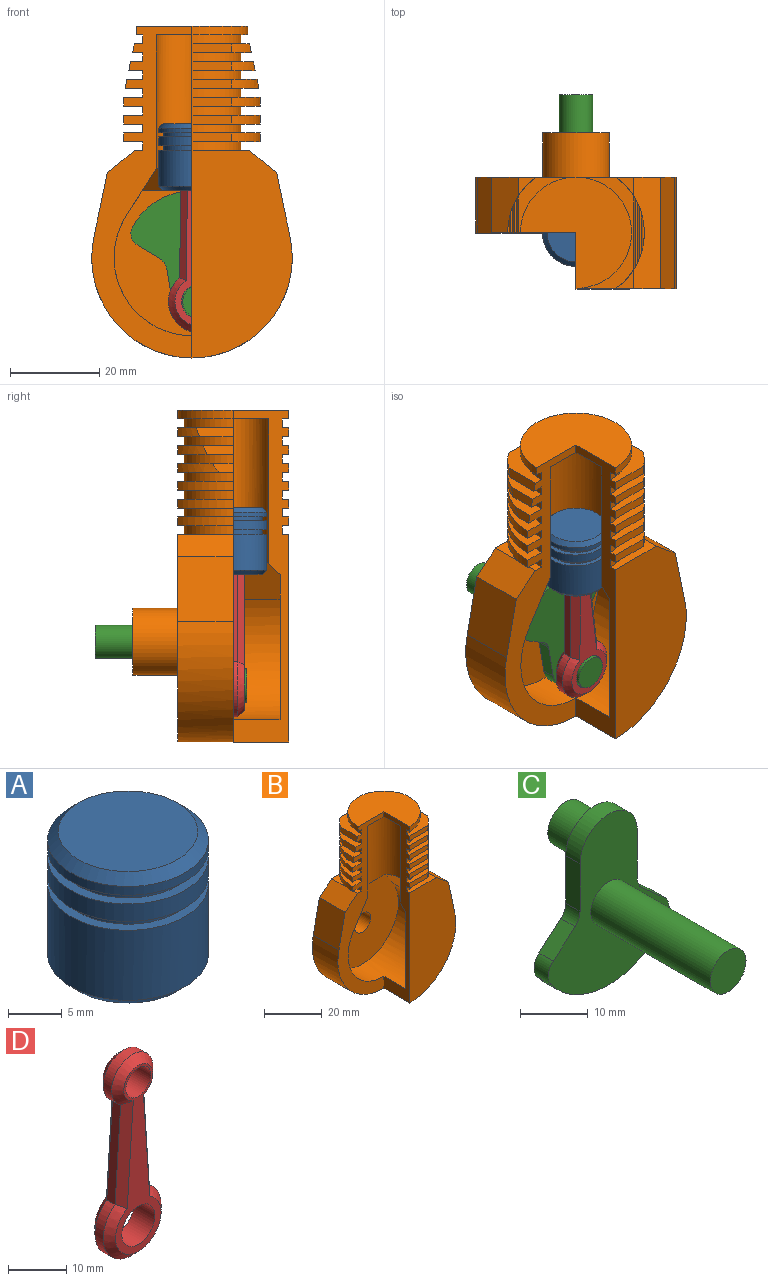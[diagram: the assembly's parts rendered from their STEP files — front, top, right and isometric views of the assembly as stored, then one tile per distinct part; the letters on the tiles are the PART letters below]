
ASSEMBLY  parts=4 mates=6
PART A: 23 faces, bbox 15x15x15 mm
  f0: plane 13x13mm, normal (0,0,-1), area 68.7mm2, adj f11,f12,f13,f14,f17,f19,f20,f21
  f1: cylinder r=7.5mm len=15mm, axis (0,0,-1), area 377mm2, adj f2,f17
  f2: plane 15x15mm, normal (0,0,1), area 44mm2, adj f1,f3
  f3: cylinder r=6.5mm len=13mm, axis (0,0,-1), area 40.8mm2, adj f2,f4
  f4: plane 15x15mm, normal (0,0,-1), area 44mm2, adj f3,f5
  f5: cylinder r=7.5mm len=15mm, axis (0,0,-1), area 94.2mm2, adj f4,f6
  f6: plane 15x15mm, normal (0,0,1), area 44mm2, adj f5,f7
  f7: cylinder r=6.5mm len=13mm, axis (0,0,-1), area 40.8mm2, adj f6,f8
  f8: plane 15x15mm, normal (0,0,-1), area 44mm2, adj f7,f9
  f9: cylinder r=7.5mm len=15mm, axis (0,0,-1), area 47.1mm2, adj f8,f18
  f10: plane 13x13mm, normal (0,0,1), area 132.7mm2, adj f18
  f11: plane 12x4mm, normal (0,1,0), area 48mm2, adj f0,f15,f21,f22
  f12: plane 12x9mm, normal (1,0,0), area 84.2mm2, adj f0,f15,f16,f20,f21
  f13: plane 12x4mm, normal (0,-1,0), area 48mm2, adj f0,f15,f19,f20
  f14: plane 12x9mm, normal (-1,0,0), area 84.2mm2, adj f0,f15,f16,f19,f22
  f15: plane 11x6mm, normal (0,0,-1), area 64mm2, adj f11,f12,f13,f14,f19,f20,f21,f22
  f16: cylinder r=2.75mm len=6mm, axis (-1,0,0), area 103.7mm2, adj f12,f14
  f17: cone r=6.5mm half-angle=45deg, axis (0,0,1), area 62.2mm2, adj f0,f1
  f18: cone r=7.5mm half-angle=45deg, axis (0,0,-1), area 62.2mm2, adj f9,f10
  f19: plane 12x1mm, normal (-0.71,-0.71,0), area 17mm2, adj f0,f13,f14,f15
  f20: plane 12x1mm, normal (0.71,-0.71,0), area 17mm2, adj f0,f12,f13,f15
  f21: plane 12x1mm, normal (0.71,0.71,0), area 17mm2, adj f0,f11,f12,f15
  f22: plane 12x1mm, normal (-0.71,0.71,0), area 17mm2, adj f0,f11,f14,f15
PART B: 80 faces, bbox 45x35x74.5 mm
  f0: plane 74.5x22.5mm, normal (0,-1,0), area 473.4mm2, adj f8,f12,f16,f19,f20,f21,f22,f23
  f1: plane 8.89x2mm, normal (0,-1,0), area 17.8mm2, adj f28,f30,f35,f59
  f2: plane 17.77x2mm, normal (0,1,0), area 35.5mm2, adj f28,f30,f59,f60
  f3: plane 8.89x2mm, normal (0,-1,0), area 17.8mm2, adj f26,f29,f35,f61
  f4: plane 17.77x2mm, normal (0,1,0), area 35.5mm2, adj f26,f29,f61,f62
  f5: plane 8.89x2mm, normal (0,-1,0), area 17.8mm2, adj f24,f27,f35,f63
  f6: plane 17.77x2mm, normal (0,1,0), area 35.5mm2, adj f24,f27,f63,f64
  f7: plane 8.89x2mm, normal (0,-1,0), area 17.8mm2, adj f22,f25,f35,f65
  f8: plane 4.7x2mm, normal (-0.98,0,0.21), area 8.1mm2, adj f0,f22,f25,f66
  f9: plane 9.4x2mm, normal (0.98,0,0.21), area 16.2mm2, adj f22,f25,f65,f67
  f10: plane 17.77x2mm, normal (0,1,0), area 35.5mm2, adj f22,f25,f66,f67
  f11: plane 8.89x2mm, normal (0,-1,0), area 17.8mm2, adj f20,f23,f35,f68
  f12: plane 6.77x2mm, normal (-0.98,0,0.21), area 12.9mm2, adj f0,f20,f23,f69
  f13: plane 13.55x2mm, normal (0.98,0,0.21), area 25.8mm2, adj f20,f23,f68,f70
  f14: plane 17.77x2mm, normal (0,1,0), area 35.5mm2, adj f20,f23,f69,f70
  f15: plane 8.89x2mm, normal (0,-1,0), area 17.8mm2, adj f19,f21,f35,f71
  f16: plane 8.26x2mm, normal (-0.98,0,0.21), area 16.2mm2, adj f0,f19,f21,f72
  f17: plane 16.53x2mm, normal (0.98,0,0.21), area 32.4mm2, adj f19,f21,f71,f73
  f18: plane 17.77x2mm, normal (0,1,0), area 35.5mm2, adj f19,f21,f72,f73
  f19: plane 25.84x25mm, normal (0,0,1), area 177mm2, adj f0,f15,f16,f17,f18,f35,f51,f71
  f20: plane 27.52x25mm, normal (0,0,1), area 196.1mm2, adj f0,f11,f12,f13,f14,f35,f52,f68
  f21: plane 26.68x25mm, normal (0,0,-1), area 187mm2, adj f0,f15,f16,f17,f18,f35,f52,f71
  f22: plane 29.2x25mm, normal (0,0,1), area 210.7mm2, adj f0,f7,f8,f9,f10,f35,f53,f65
  f23: plane 28.36x25mm, normal (0,0,-1), area 204mm2, adj f0,f11,f12,f13,f14,f35,f53,f68
  f24: plane 30.67x25mm, normal (0,0,1), area 217.7mm2, adj f0,f5,f6,f35,f54,f63,f64
  f25: plane 30.04x25mm, normal (0,0,-1), area 215.7mm2, adj f0,f7,f8,f9,f10,f35,f54,f65
  f26: plane 30.67x25mm, normal (0,0,1), area 217.7mm2, adj f0,f3,f4,f35,f55,f61,f62
  f27: plane 30.67x25mm, normal (0,0,-1), area 217.7mm2, adj f0,f5,f6,f35,f55,f63,f64
  f28: plane 30.67x25mm, normal (0,0,1), area 217.7mm2, adj f0,f1,f2,f35,f56,f59,f60
  f29: plane 30.67x25mm, normal (0,0,-1), area 217.7mm2, adj f0,f3,f4,f35,f56,f61,f62
  f30: plane 30.67x25mm, normal (0,0,-1), area 217.7mm2, adj f0,f1,f2,f35,f57,f59,f60
  f31: plane 46.5x22.5mm, normal (0,-1,0), area 875.9mm2, adj f33,f35,f45,f58,f75
  f32: plane 14.49x12.5mm, normal (-0.98,0,0.21), area 185mm2, adj f0,f34,f45,f74
  f33: plane 25x14.49mm, normal (0.98,0,0.21), area 370.1mm2, adj f31,f34,f45,f75
  f34: plane 46.5x45mm, normal (0,1,0), area 1575.2mm2, adj f32,f33,f43,f45,f58,f74,f75
  f35: plane 74.5x12.5mm, normal (-1,0,0), area 285.8mm2, adj f0,f1,f3,f5,f7,f11,f15,f19
  f36: plane 5.5x2.19mm, normal (0,0,-1), area 3.8mm2, adj f39,f42,f50
  f37: plane 5.5x2.19mm, normal (0,0,-1), area 3.8mm2, adj f38,f42,f49
  f38: plane 21x10.59mm, normal (-0.84,0,-0.54), area 234.1mm2, adj f37,f40,f46,f47,f48,f49,f50
  f39: plane 10.59x10.5mm, normal (0.84,0,-0.54), area 117.1mm2, adj f0,f36,f40,f47,f50
  f40: cylinder r=17.5mm len=35mm, axis (0,-1,0), area 1178.9mm2, adj f0,f35,f38,f39,f47,f48
  f41: cylinder r=4mm len=12mm, axis (0,1,0), area 301.6mm2, adj f44,f47
  f42: cylinder r=8mm len=32.51mm, axis (0,0,1), area 1163.1mm2, adj f0,f35,f36,f37,f46,f49,f50,f76
  f43: cylinder r=7.5mm len=15mm, axis (0,1,0), area 471.2mm2, adj f34,f44
  f44: plane 15x15mm, normal (0,1,0), area 126.4mm2, adj f41,f43
  f45: cylinder r=22.5mm len=45mm, axis (0,1,0), area 1499.8mm2, adj f0,f31,f32,f33,f34,f35
  f46: plane 5.5x2.19mm, normal (0,0,-1), area 3.8mm2, adj f38,f42,f50
  f47: plane 35x32.5mm, normal (0,-1,0), area 888.5mm2, adj f38,f39,f40,f41,f50
  f48: plane 32.5x17.5mm, normal (0,1,0), area 469.4mm2, adj f35,f38,f40,f49
  f49: plane 11.19x5mm, normal (0,0.71,-0.71), area 53.7mm2, adj f35,f37,f38,f42,f48
  f50: plane 22.38x5mm, normal (0,-0.71,-0.71), area 107.3mm2, adj f36,f38,f39,f42,f46,f47
  f51: cylinder r=11mm len=22mm, axis (0,0,1), area 103.7mm2, adj f0,f19,f35,f79
  f52: cylinder r=11mm len=22mm, axis (0,0,1), area 103.7mm2, adj f0,f20,f21,f35
  f53: cylinder r=11mm len=22mm, axis (0,0,1), area 103.7mm2, adj f0,f22,f23,f35
  f54: cylinder r=11mm len=22mm, axis (0,0,1), area 103.7mm2, adj f0,f24,f25,f35
  f55: cylinder r=11mm len=22mm, axis (0,0,1), area 103.7mm2, adj f0,f26,f27,f35
  f56: cylinder r=11mm len=22mm, axis (0,0,1), area 103.7mm2, adj f0,f28,f29,f35
  f57: cylinder r=11mm len=22mm, axis (0,0,1), area 103.7mm2, adj f0,f30,f35,f58
  f58: plane 25.91x25mm, normal (0,0,1), area 200.7mm2, adj f0,f31,f34,f35,f57,f74,f75
  f59: cylinder r=15.34mm len=25mm, axis (0,0,1), area 58.5mm2, adj f1,f2,f28,f30
  f60: cylinder r=15.34mm len=12.5mm, axis (0,0,1), area 29.2mm2, adj f0,f2,f28,f30
  f61: cylinder r=15.34mm len=25mm, axis (0,0,1), area 58.5mm2, adj f3,f4,f26,f29
  f62: cylinder r=15.34mm len=12.5mm, axis (0,0,1), area 29.2mm2, adj f0,f4,f26,f29
  f63: cylinder r=15.34mm len=25mm, axis (0,0,1), area 58.5mm2, adj f5,f6,f24,f27
  f64: cylinder r=15.34mm len=12.5mm, axis (0,0,1), area 29.2mm2, adj f0,f6,f24,f27
  f65: cylinder r=15.34mm len=9.39mm, axis (0,0,1), area 21.2mm2, adj f7,f9,f22,f25
  f66: cylinder r=15.34mm len=9.39mm, axis (0,0,1), area 21.2mm2, adj f8,f10,f22,f25
  f67: cylinder r=15.34mm len=9.39mm, axis (0,0,1), area 21.2mm2, adj f9,f10,f22,f25
  f68: cylinder r=15.34mm len=6.65mm, axis (0,0,1), area 16.2mm2, adj f11,f13,f20,f23
  f69: cylinder r=15.34mm len=6.65mm, axis (0,0,1), area 16.2mm2, adj f12,f14,f20,f23
  f70: cylinder r=15.34mm len=6.65mm, axis (0,0,1), area 16.2mm2, adj f13,f14,f20,f23
  f71: cylinder r=15.34mm len=4.93mm, axis (0,0,1), area 12.6mm2, adj f15,f17,f19,f21
  f72: cylinder r=15.34mm len=4.93mm, axis (0,0,1), area 12.6mm2, adj f16,f18,f19,f21
  f73: cylinder r=15.34mm len=4.93mm, axis (0,0,1), area 12.6mm2, adj f17,f18,f19,f21
  f74: plane 12.5x6.03mm, normal (-0.63,0,0.78), area 97mm2, adj f0,f32,f34,f58
  f75: plane 25x6.03mm, normal (0.63,0,0.78), area 194.1mm2, adj f31,f33,f34,f58
  f76: plane 16x16mm, normal (0,0,-1), area 150.8mm2, adj f0,f35,f42
  f77: cylinder r=12.48mm len=24.97mm, axis (0,0,-1), area 117.7mm2, adj f0,f35,f78,f79
  f78: plane 24.97x24.97mm, normal (0,0,1), area 367.2mm2, adj f0,f35,f77
  f79: plane 24.97x24.97mm, normal (0,0,-1), area 82.1mm2, adj f0,f35,f51,f77
PART C: 16 faces, bbox 25.3x34x31 mm
  f0: cylinder r=3.75mm len=7.5mm, axis (0,1,0), area 141.4mm2, adj f1,f9
  f1: plane 7.5x7.5mm, normal (0,1,0), area 44.2mm2, adj f0
  f2: plane 8.63x3mm, normal (-1,0,0), area 25.9mm2, adj f7,f8,f9,f12
  f3: plane 4.58x3.99mm, normal (-0.66,0,0.75), area 18.2mm2, adj f8,f9,f12,f14
  f4: cylinder r=15mm len=24.1mm, axis (0,1,0), area 84mm2, adj f8,f9,f14,f15
  f5: plane 4.58x3.99mm, normal (0.66,0,0.75), area 18.2mm2, adj f8,f9,f13,f15
  f6: plane 8.63x3mm, normal (1,0,0), area 25.9mm2, adj f7,f8,f9,f13
  f7: cylinder r=6mm len=12mm, axis (0,1,0), area 56.5mm2, adj f2,f6,f8,f9
  f8: plane 31x25.28mm, normal (0,-1,0), area 421.4mm2, adj f2,f3,f4,f5,f6,f7,f10,f12
  f9: plane 31x25.28mm, normal (0,1,0), area 421.4mm2, adj f0,f2,f3,f4,f5,f6,f7,f12
  f10: cylinder r=3.75mm len=25mm, axis (0,1,0), area 589mm2, adj f8,f11
  f11: plane 7.5x7.5mm, normal (0,-1,0), area 44.2mm2, adj f10
  f12: cylinder r=3mm len=3mm, axis (0,-1,0), area 7.7mm2, adj f2,f3,f8,f9
  f13: cylinder r=3mm len=3mm, axis (0,-1,0), area 7.7mm2, adj f5,f6,f8,f9
  f14: cylinder r=3mm len=4.05mm, axis (0,1,0), area 13.4mm2, adj f3,f4,f8,f9
  f15: cylinder r=3mm len=4.05mm, axis (0,1,0), area 13.4mm2, adj f4,f5,f8,f9
PART D: 16 faces, bbox 14.1x5.1x42.1 mm
  f0: plane 20.2x2mm, normal (-1,0,0.07), area 40.5mm2, adj f1,f4,f11,f15
  f1: cylinder r=7mm len=14mm, axis (0,1,0), area 70.3mm2, adj f0,f2,f10,f14
  f2: plane 20.2x2mm, normal (1,0,0.07), area 40.5mm2, adj f1,f4,f8,f12
  f3: cylinder r=3mm len=6mm, axis (0,1,0), area 94.2mm2, adj f6,f7
  f4: cylinder r=5mm len=10mm, axis (0,1,0), area 51mm2, adj f0,f2,f9,f13
  f5: cylinder r=4mm len=8mm, axis (0,1,0), area 125.7mm2, adj f6,f7
  f6: plane 39x11mm, normal (0,-1,0), area 137.7mm2, adj f3,f5,f12,f13,f14,f15
  f7: plane 39x11mm, normal (0,1,0), area 137.7mm2, adj f3,f5,f8,f9,f10,f11
  f8: plane 22.06x3.05mm, normal (0.71,0.71,0.05), area 44.7mm2, adj f2,f7,f9,f10
  f9: cone r=5mm half-angle=45deg, axis (0,-1,0), area 48mm2, adj f4,f7,f8,f11
  f10: cone r=7mm half-angle=45deg, axis (0,-1,0), area 68.1mm2, adj f1,f7,f8,f11
  f11: plane 22.06x3.05mm, normal (-0.71,0.71,0.05), area 44.7mm2, adj f0,f7,f9,f10
  f12: plane 22.06x3.05mm, normal (0.71,-0.71,0.05), area 44.7mm2, adj f2,f6,f13,f14
  f13: cone r=3.5mm half-angle=45deg, axis (0,1,0), area 48mm2, adj f4,f6,f12,f15
  f14: cone r=5.5mm half-angle=45deg, axis (0,1,0), area 68.1mm2, adj f1,f6,f12,f15
  f15: plane 22.06x3.05mm, normal (-0.71,-0.71,0.05), area 44.7mm2, adj f0,f6,f13,f14
PLACE A rot(axis=(0,0,1),90deg) t=(-0.42,-32,11.25)mm
PLACE B t=(-0.42,-9.5,-12.85)mm fixed
PLACE C rot(axis=(-1,0,-0.08),180deg) t=(1.26,-35,-22.7)mm
PLACE D rot(axis=(-0.03,0,1),180deg) t=(1.26,-34.5,-22.7)mm
MATE planar D.f6 <-> C.f4  axis (0,1,0) through (0.65,-29.5,-11.71)mm
MATE cylindrical C.f4 <-> B.f41  axis (0,-1,0) through (-0.42,-13.5,-12.85)mm
MATE cylindrical D.f5 <-> C.f0  axis (0,-1,0) through (1.26,-32,-22.7)mm
MATE planar D.f7 <-> A.f16  axis (0,-1,0) through (0.65,-34.5,-11.71)mm
MATE cylindrical A.f1 <-> B.f42  axis (0,0,-1) through (-0.42,-32,7.25)mm
MATE cylindrical A.f16 <-> D.f3  axis (0,-1,0) through (-0.42,-32,7.25)mm
